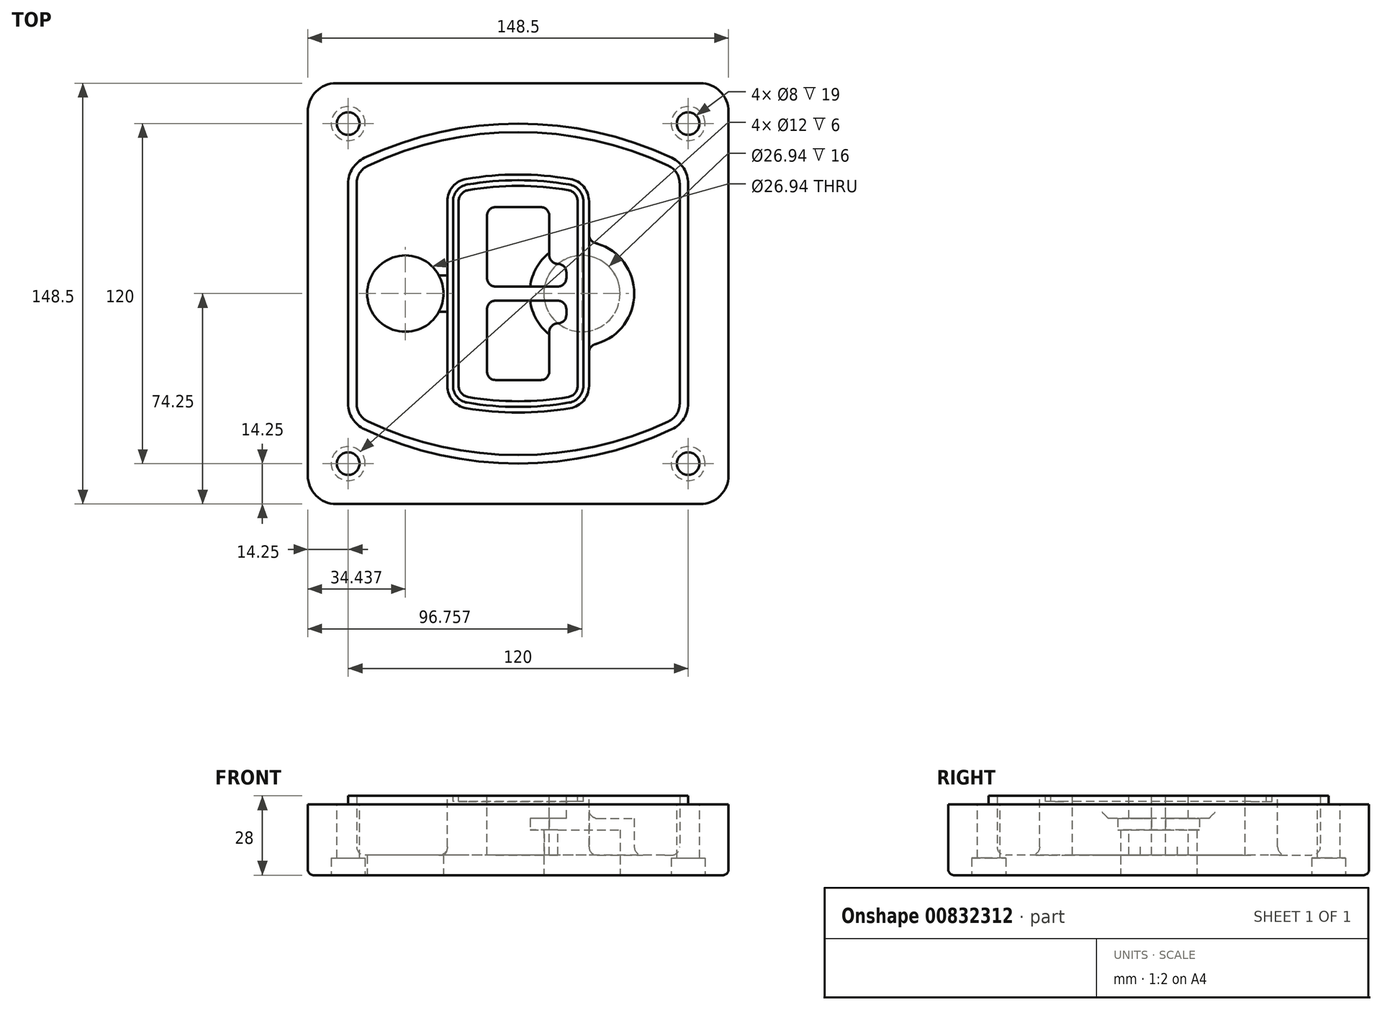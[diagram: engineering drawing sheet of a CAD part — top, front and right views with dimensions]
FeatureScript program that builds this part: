
annotation { "Feature Type Name" : "Feature", "Feature Type Description" : "" }
export const myFeature = defineFeature(function(context is Context, id is Id, definition is map)
    precondition{}
    {
        {
            var Q0;
            Q0=qCreatedBy(makeId("Top.planeOp"),FACE);
            var sketch = newSketch(context, id + "F0", { "sketchPlane" : qUnion([Q0])});
            skPoint(sketch, "E0.rect.middle", {"position": v(0, 0) * mm});
            skLineSegment(sketch, "E1.bottom", {"start": v(-64.25, -74.25) * mm, "end": v(64.25, -74.25) * mm});
            skLineSegment(sketch, "E1.top", {"start": v(-64.25, 74.25) * mm, "end": v(64.25, 74.25) * mm});
            skLineSegment(sketch, "E1.left", {"start": v(-74.25, -64.25) * mm, "end": v(-74.25, 64.25) * mm});
            skLineSegment(sketch, "E1.right", {"start": v(74.25, -64.25) * mm, "end": v(74.25, 64.25) * mm});
            skLineSegment(sketch, "E2", {"start": v(-74.25, 74.25) * mm, "end": v(74.25, -74.25) * mm, "construction": true});
            skLineSegment(sketch, "E3", {"start": v(74.25, 74.25) * mm, "end": v(-74.25, -74.25) * mm, "construction": true});
            skCircle(sketch, "E4", {"center": v(-60, 60) * mm, "radius": 4 * mm});
            skCircle(sketch, "E5", {"center": v(60, 60) * mm, "radius": 4 * mm});
            skCircle(sketch, "E6", {"center": v(60, -60) * mm, "radius": 4 * mm});
            skCircle(sketch, "E7", {"center": v(-60, -60) * mm, "radius": 4 * mm});
            skLineSegment(sketch, "E8", {"start": v(-60, 60) * mm, "end": v(60, 60) * mm, "construction": true});
            skLineSegment(sketch, "E9", {"start": v(60, 60) * mm, "end": v(60, -60) * mm, "construction": true});
            skLineSegment(sketch, "E10", {"start": v(60, -60) * mm, "end": v(-60, -60) * mm, "construction": true});
            skLineSegment(sketch, "E11", {"start": v(-60, -60) * mm, "end": v(-60, 60) * mm, "construction": true});
            skLineSegment(sketch, "E12", {"start": v(-60, 38.83) * mm, "end": v(-60, -38.83) * mm});
            skLineSegment(sketch, "E13", {"start": v(60, 38.83) * mm, "end": v(60, -38.83) * mm});
            skArc(sketch, "E14", {"start": v(54.26, 47.88) * mm, "mid": v(0, 60) * mm, "end": v(-54.26, 47.88) * mm});
            skArc(sketch, "E15", {"start": v(-54.26, -47.88) * mm, "mid": v(0, -60) * mm, "end": v(54.26, -47.88) * mm});
            skLineSegment(sketch, "E16", {"start": v(-60, 0) * mm, "end": v(60, 0) * mm, "construction": true});
            skPoint(sketch, "E17.visualSharp", {"position": v(-60, -45) * mm});
            skArc(sketch, "E17.filletArc", {"start": v(-60, -38.83) * mm, "mid": v(-58.44, -44.2) * mm, "end": v(-54.26, -47.88) * mm});
            skPoint(sketch, "E18.visualSharp", {"position": v(-60, 45) * mm});
            skArc(sketch, "E18.filletArc", {"start": v(-54.26, 47.88) * mm, "mid": v(-58.44, 44.2) * mm, "end": v(-60, 38.83) * mm});
            skPoint(sketch, "E19.visualSharp", {"position": v(60, 45) * mm});
            skArc(sketch, "E19.filletArc", {"start": v(60, 38.83) * mm, "mid": v(58.44, 44.2) * mm, "end": v(54.26, 47.88) * mm});
            skPoint(sketch, "E20.visualSharp", {"position": v(60, -45) * mm});
            skArc(sketch, "E20.filletArc", {"start": v(54.26, -47.88) * mm, "mid": v(58.44, -44.2) * mm, "end": v(60, -38.83) * mm});
            skPoint(sketch, "E21.visualSharp", {"position": v(-74.25, 74.25) * mm});
            skArc(sketch, "E21.filletArc", {"start": v(-64.25, 74.25) * mm, "mid": v(-71.32, 71.32) * mm, "end": v(-74.25, 64.25) * mm});
            skPoint(sketch, "E22.visualSharp", {"position": v(74.25, 74.25) * mm});
            skArc(sketch, "E22.filletArc", {"start": v(74.25, 64.25) * mm, "mid": v(71.32, 71.32) * mm, "end": v(64.25, 74.25) * mm});
            skPoint(sketch, "E23.visualSharp", {"position": v(74.25, -74.25) * mm});
            skArc(sketch, "E23.filletArc", {"start": v(64.25, -74.25) * mm, "mid": v(71.32, -71.32) * mm, "end": v(74.25, -64.25) * mm});
            skPoint(sketch, "E24.visualSharp", {"position": v(-74.25, -74.25) * mm});
            skArc(sketch, "E24.filletArc", {"start": v(-74.25, -64.25) * mm, "mid": v(-71.32, -71.32) * mm, "end": v(-64.25, -74.25) * mm});
            skArc(sketch, "E25.0", {"start": v(57, 38.83) * mm, "mid": v(55.9, 42.58) * mm, "end": v(52.98, 45.17) * mm});
            skLineSegment(sketch, "E25.1", {"start": v(57, 38.83) * mm, "end": v(57, -38.83) * mm});
            skArc(sketch, "E25.2", {"start": v(52.98, -45.17) * mm, "mid": v(55.9, -42.58) * mm, "end": v(57, -38.83) * mm});
            skArc(sketch, "E25.3", {"start": v(-52.98, -45.17) * mm, "mid": v(0, -57) * mm, "end": v(52.98, -45.17) * mm});
            skArc(sketch, "E25.4", {"start": v(-57, -38.83) * mm, "mid": v(-55.9, -42.58) * mm, "end": v(-52.98, -45.17) * mm});
            skArc(sketch, "E25.5", {"start": v(52.98, 45.17) * mm, "mid": v(0, 57) * mm, "end": v(-52.98, 45.17) * mm});
            skLineSegment(sketch, "E25.6", {"start": v(-57, 38.83) * mm, "end": v(-57, -38.83) * mm});
            skArc(sketch, "E25.7", {"start": v(-52.98, 45.17) * mm, "mid": v(-55.9, 42.58) * mm, "end": v(-57, 38.83) * mm});
            skArc(sketch, "E26.0", {"start": v(-55.96, 51.5) * mm, "mid": v(-61.82, 46.33) * mm, "end": v(-64, 38.83) * mm});
            skArc(sketch, "E26.1", {"start": v(55.96, 51.5) * mm, "mid": v(0, 64) * mm, "end": v(-55.96, 51.5) * mm});
            skArc(sketch, "E26.2", {"start": v(64, 38.83) * mm, "mid": v(61.82, 46.33) * mm, "end": v(55.96, 51.5) * mm});
            skLineSegment(sketch, "E26.3", {"start": v(64, 38.83) * mm, "end": v(64, -38.83) * mm});
            skArc(sketch, "E26.4", {"start": v(55.96, -51.5) * mm, "mid": v(61.82, -46.33) * mm, "end": v(64, -38.83) * mm});
            skLineSegment(sketch, "E26.5", {"start": v(-64, 38.83) * mm, "end": v(-64, -38.83) * mm});
            skArc(sketch, "E26.6", {"start": v(-55.96, -51.5) * mm, "mid": v(0, -64) * mm, "end": v(55.96, -51.5) * mm});
            skArc(sketch, "E26.7", {"start": v(-64, -38.83) * mm, "mid": v(-61.82, -46.33) * mm, "end": v(-55.96, -51.5) * mm});
            skSolve(sketch);
        }
        {
            var Q0;
            Q0=makeQuery(id+"F0.imprint","IMPRINT",FACE,{"disambiguationData":[TD([[makeQuery(id+"F0.imprint","IMPRINT",EDGE,{"derivedFrom":sQuery(id+"F0.wireOp",EDGE,"E1.bottom")}),1.0]])]});
            var Q1;
            Q1=makeQuery(id+"F0.imprint","IMPRINT",FACE,{"disambiguationData":[TD([[makeQuery(id+"F0.imprint","IMPRINT",EDGE,{"derivedFrom":sQuery(id+"F0.wireOp",EDGE,"E12")}),1.0]])]});
            var Q2;
            Q2=makeQuery(id+"F0.imprint","IMPRINT",FACE,{"disambiguationData":[TD([[makeQuery(id+"F0.imprint","IMPRINT",EDGE,{"derivedFrom":sQuery(id+"F0.wireOp",EDGE,"E25.0")}),1.0]])]});
            var Q3;
            Q3=makeQuery(id+"F0.imprint","IMPRINT",FACE,{"disambiguationData":[TD([[makeQuery(id+"F0.imprint","IMPRINT",EDGE,{"derivedFrom":sQuery(id+"F0.wireOp",EDGE,"E12")}),-1.0]])]});
            extrude(context, id + "F1", {"entities" : qUnion([Q0, Q1, Q2, Q3]), "oppositeDirection" : true, "depth" : 25 * mm});
        }
        {
            var Q0;
            Q0=makeQuery(id+"F0.imprint","IMPRINT",FACE,{"disambiguationData":[TD([[makeQuery(id+"F0.imprint","IMPRINT",EDGE,{"derivedFrom":sQuery(id+"F0.wireOp",EDGE,"E12")}),1.0]])]});
            extrude(context, id + "F2", {"entities" : qUnion([Q0]), "operationType" : NewBodyOperationType.ADD, "depth" : 3 * mm, "offsetDistance" : 25 * mm});
        }
        {
            var Q0;
            Q0=makeQuery(id+"F0.imprint","IMPRINT",FACE,{"disambiguationData":[TD([[makeQuery(id+"F0.imprint","IMPRINT",EDGE,{"derivedFrom":sQuery(id+"F0.wireOp",EDGE,"E25.0")}),1.0]])]});
            extrude(context, id + "F3", {"entities" : qUnion([Q0]), "operationType" : NewBodyOperationType.REMOVE, "oppositeDirection" : true, "depth" : 18 * mm});
        }
        {
            var Q0;
            Q0=makeQuery(id+"F2.opExtrude","CAP_FACE",FACE,{"disambiguationData":[OSD([sQuery(id+"F0.wireOp",EDGE,"E12"),sQuery(id+"F0.wireOp",EDGE,"E13"),sQuery(id+"F0.wireOp",EDGE,"E14"),sQuery(id+"F0.wireOp",EDGE,"E15"),sQuery(id+"F0.wireOp",EDGE,"E17.filletArc"),sQuery(id+"F0.wireOp",EDGE,"E18.filletArc"),sQuery(id+"F0.wireOp",EDGE,"E19.filletArc"),sQuery(id+"F0.wireOp",EDGE,"E20.filletArc"),sQuery(id+"F0.wireOp",EDGE,"E25.0"),sQuery(id+"F0.wireOp",EDGE,"E25.1"),sQuery(id+"F0.wireOp",EDGE,"E25.2"),sQuery(id+"F0.wireOp",EDGE,"E25.3"),sQuery(id+"F0.wireOp",EDGE,"E25.4"),sQuery(id+"F0.wireOp",EDGE,"E25.5"),sQuery(id+"F0.wireOp",EDGE,"E25.6"),sQuery(id+"F0.wireOp",EDGE,"E25.7")])],"isStart":false});
            var sketch = newSketch(context, id + "F4", { "sketchPlane" : qUnion([Q0])});
            skArc(sketch, "E27.0", {"start": v(-18.34, -40.45) * mm, "mid": v(0, -42) * mm, "end": v(18.34, -40.45) * mm});
            skArc(sketch, "E28.0", {"start": v(18.34, 40.45) * mm, "mid": v(0, 42) * mm, "end": v(-18.34, 40.45) * mm});
            skLineSegment(sketch, "E29", {"start": v(-25, 32.57) * mm, "end": v(-25, -32.57) * mm});
            skLineSegment(sketch, "E30", {"start": v(25, 32.57) * mm, "end": v(25, -32.57) * mm});
            skLineSegment(sketch, "E31", {"start": v(-25, 39.1) * mm, "end": v(25, 39.1) * mm, "construction": true});
            skLineSegment(sketch, "E32", {"start": v(-25, -39.1) * mm, "end": v(25, -39.1) * mm, "construction": true});
            skPoint(sketch, "E33.visualSharp", {"position": v(-25, 39.1) * mm});
            skArc(sketch, "E33.filletArc", {"start": v(-18.34, 40.45) * mm, "mid": v(-23.11, 37.73) * mm, "end": v(-25, 32.57) * mm});
            skPoint(sketch, "E34.visualSharp", {"position": v(25, 39.1) * mm});
            skArc(sketch, "E34.filletArc", {"start": v(25, 32.57) * mm, "mid": v(23.11, 37.73) * mm, "end": v(18.34, 40.45) * mm});
            skPoint(sketch, "E35.visualSharp", {"position": v(25, -39.1) * mm});
            skArc(sketch, "E35.filletArc", {"start": v(18.34, -40.45) * mm, "mid": v(23.11, -37.73) * mm, "end": v(25, -32.57) * mm});
            skPoint(sketch, "E36.visualSharp", {"position": v(-25, -39.1) * mm});
            skArc(sketch, "E36.filletArc", {"start": v(-25, -32.57) * mm, "mid": v(-23.11, -37.73) * mm, "end": v(-18.34, -40.45) * mm});
            skArc(sketch, "E37.0", {"start": v(52.98, 45.17) * mm, "mid": v(0, 57) * mm, "end": v(-52.98, 45.17) * mm});
            skArc(sketch, "E37.1", {"start": v(-52.98, 45.17) * mm, "mid": v(-55.9, 42.58) * mm, "end": v(-57, 38.83) * mm});
            skLineSegment(sketch, "E37.2", {"start": v(-57, 38.83) * mm, "end": v(-57, -38.83) * mm});
            skArc(sketch, "E37.3", {"start": v(-57, -38.83) * mm, "mid": v(-55.9, -42.58) * mm, "end": v(-52.98, -45.17) * mm});
            skArc(sketch, "E37.4", {"start": v(-52.98, -45.17) * mm, "mid": v(0, -57) * mm, "end": v(52.98, -45.17) * mm});
            skArc(sketch, "E37.5", {"start": v(52.98, -45.17) * mm, "mid": v(55.9, -42.58) * mm, "end": v(57, -38.83) * mm});
            skLineSegment(sketch, "E37.6", {"start": v(57, 38.83) * mm, "end": v(57, -38.83) * mm});
            skArc(sketch, "E37.7", {"start": v(57, 38.83) * mm, "mid": v(55.9, 42.58) * mm, "end": v(52.98, 45.17) * mm});
            skLineSegment(sketch, "E38.0", {"start": v(23, 32.57) * mm, "end": v(23, -32.57) * mm});
            skArc(sketch, "E38.1", {"start": v(18, -38.48) * mm, "mid": v(21.58, -36.44) * mm, "end": v(23, -32.57) * mm});
            skArc(sketch, "E38.2", {"start": v(-18, -38.48) * mm, "mid": v(0, -40) * mm, "end": v(18, -38.48) * mm});
            skArc(sketch, "E38.3", {"start": v(-23, -32.57) * mm, "mid": v(-21.58, -36.44) * mm, "end": v(-18, -38.48) * mm});
            skLineSegment(sketch, "E38.4", {"start": v(-23, 32.57) * mm, "end": v(-23, -32.57) * mm});
            skArc(sketch, "E38.5", {"start": v(23, 32.57) * mm, "mid": v(21.58, 36.44) * mm, "end": v(18, 38.48) * mm});
            skArc(sketch, "E38.6", {"start": v(-18, 38.48) * mm, "mid": v(-21.58, 36.44) * mm, "end": v(-23, 32.57) * mm});
            skArc(sketch, "E38.7", {"start": v(18, 38.48) * mm, "mid": v(0, 40) * mm, "end": v(-18, 38.48) * mm});
            skArc(sketch, "E39.0", {"start": v(21, 32.57) * mm, "mid": v(20.06, 35.15) * mm, "end": v(17.67, 36.5) * mm});
            skLineSegment(sketch, "E39.1", {"start": v(21, 32.57) * mm, "end": v(21, -32.57) * mm});
            skArc(sketch, "E39.2", {"start": v(17.67, -36.5) * mm, "mid": v(20.06, -35.15) * mm, "end": v(21, -32.57) * mm});
            skArc(sketch, "E39.3", {"start": v(-17.67, -36.5) * mm, "mid": v(0, -38) * mm, "end": v(17.67, -36.5) * mm});
            skArc(sketch, "E39.4", {"start": v(-21, -32.57) * mm, "mid": v(-20.06, -35.15) * mm, "end": v(-17.67, -36.5) * mm});
            skArc(sketch, "E39.5", {"start": v(17.67, 36.5) * mm, "mid": v(0, 38) * mm, "end": v(-17.67, 36.5) * mm});
            skLineSegment(sketch, "E39.6", {"start": v(-21, 32.57) * mm, "end": v(-21, -32.57) * mm});
            skArc(sketch, "E39.7", {"start": v(-17.67, 36.5) * mm, "mid": v(-20.06, 35.15) * mm, "end": v(-21, 32.57) * mm});
            skLineSegment(sketch, "E40", {"start": v(-25, 0) * mm, "end": v(25, 0) * mm, "construction": true});
            skLineSegment(sketch, "E41", {"start": v(-11, 5.5) * mm, "end": v(-11, 27.5) * mm});
            skLineSegment(sketch, "E42", {"start": v(-8, 30.5) * mm, "end": v(8, 30.5) * mm});
            skLineSegment(sketch, "E43", {"start": v(11, 27.5) * mm, "end": v(11, 13.5) * mm});
            skLineSegment(sketch, "E44", {"start": v(14, 10.5) * mm, "end": v(14, 10.5) * mm});
            skLineSegment(sketch, "E45", {"start": v(17, 7.5) * mm, "end": v(17, 5.5) * mm});
            skLineSegment(sketch, "E46", {"start": v(14, 2.5) * mm, "end": v(-8, 2.5) * mm});
            skPoint(sketch, "E47.visualSharp", {"position": v(-11, 30.5) * mm});
            skArc(sketch, "E47.filletArc", {"start": v(-8, 30.5) * mm, "mid": v(-10.12, 29.62) * mm, "end": v(-11, 27.5) * mm});
            skPoint(sketch, "E48.visualSharp", {"position": v(11, 30.5) * mm});
            skArc(sketch, "E48.filletArc", {"start": v(11, 27.5) * mm, "mid": v(10.12, 29.62) * mm, "end": v(8, 30.5) * mm});
            skPoint(sketch, "E49.visualSharp", {"position": v(11, 10.5) * mm});
            skArc(sketch, "E49.filletArc", {"start": v(11, 13.5) * mm, "mid": v(11.88, 11.38) * mm, "end": v(14, 10.5) * mm});
            skPoint(sketch, "E50.visualSharp", {"position": v(17, 10.5) * mm});
            skArc(sketch, "E50.filletArc", {"start": v(17, 7.5) * mm, "mid": v(16.12, 9.62) * mm, "end": v(14, 10.5) * mm});
            skPoint(sketch, "E51.visualSharp", {"position": v(17, 2.5) * mm});
            skArc(sketch, "E51.filletArc", {"start": v(14, 2.5) * mm, "mid": v(16.12, 3.38) * mm, "end": v(17, 5.5) * mm});
            skPoint(sketch, "E52.visualSharp", {"position": v(-11, 2.5) * mm});
            skArc(sketch, "E52.filletArc", {"start": v(-11, 5.5) * mm, "mid": v(-10.12, 3.38) * mm, "end": v(-8, 2.5) * mm});
            skLineSegment(sketch, "E53.0.MirrorCS", {"start": v(14, -2.5) * mm, "end": v(-8, -2.5) * mm});
            skArc(sketch, "E54.0.MirrorCS", {"start": v(-11, -5.5) * mm, "mid": v(-10.12, -3.38) * mm, "end": v(-8, -2.5) * mm});
            skLineSegment(sketch, "E55.0.MirrorCS", {"start": v(-11, -5.5) * mm, "end": v(-11, -27.5) * mm});
            skArc(sketch, "E56.0.MirrorCS", {"start": v(-8, -30.5) * mm, "mid": v(-10.12, -29.62) * mm, "end": v(-11, -27.5) * mm});
            skLineSegment(sketch, "E57.0.MirrorCS", {"start": v(-8, -30.5) * mm, "end": v(8, -30.5) * mm});
            skArc(sketch, "E58.0.MirrorCS", {"start": v(11, -27.5) * mm, "mid": v(10.12, -29.62) * mm, "end": v(8, -30.5) * mm});
            skLineSegment(sketch, "E59.0.MirrorCS", {"start": v(11, -27.5) * mm, "end": v(11, -13.5) * mm});
            skArc(sketch, "E60.0.MirrorCS", {"start": v(11, -13.5) * mm, "mid": v(11.88, -11.38) * mm, "end": v(14, -10.5) * mm});
            skArc(sketch, "E61.0.MirrorCS", {"start": v(17, -7.5) * mm, "mid": v(16.12, -9.62) * mm, "end": v(14, -10.5) * mm});
            skLineSegment(sketch, "E62.0.MirrorCS", {"start": v(17, -7.5) * mm, "end": v(17, -5.5) * mm});
            skArc(sketch, "E63.0.MirrorCS", {"start": v(14, -2.5) * mm, "mid": v(16.12, -3.38) * mm, "end": v(17, -5.5) * mm});
            skSolve(sketch);
        }
        {
            var Q0;
            Q0=makeQuery(id+"F4.imprint","IMPRINT",FACE,{"disambiguationData":[TD([[makeQuery(id+"F4.imprint","IMPRINT",EDGE,{"derivedFrom":sQuery(id+"F4.wireOp",EDGE,"E27.0")}),1.0]])]});
            var Q1;
            Q1=makeQuery(id+"F4.imprint","IMPRINT",FACE,{"disambiguationData":[TD([[makeQuery(id+"F4.imprint","IMPRINT",EDGE,{"derivedFrom":sQuery(id+"F4.wireOp",EDGE,"E38.0")}),-1.0]])]});
            var Q2;
            Q2=makeQuery(id+"F4.imprint","IMPRINT",FACE,{"disambiguationData":[TD([[makeQuery(id+"F4.imprint","IMPRINT",EDGE,{"derivedFrom":sQuery(id+"F4.wireOp",EDGE,"E39.0")}),1.0]])]});
            extrude(context, id + "F5", {"entities" : qUnion([Q0, Q1, Q2]), "operationType" : NewBodyOperationType.ADD, "endBound" : BoundingType.UP_TO_NEXT, "oppositeDirection" : true, "depth" : 25 * mm});
        }
        {
            var Q0;
            Q0=makeQuery(id+"F4.imprint","IMPRINT",FACE,{"disambiguationData":[TD([[makeQuery(id+"F4.imprint","IMPRINT",EDGE,{"derivedFrom":sQuery(id+"F4.wireOp",EDGE,"E38.0")}),-1.0]])]});
            extrude(context, id + "F6", {"entities" : qUnion([Q0]), "operationType" : NewBodyOperationType.REMOVE, "oppositeDirection" : true, "depth" : 2 * mm});
        }
        {
            var Q0;
            Q0=makeQuery(id+"F1.opExtrude","CAP_FACE",FACE,{"disambiguationData":[OSD([sQuery(id+"F0.wireOp",EDGE,"E1.bottom"),sQuery(id+"F0.wireOp",EDGE,"E1.top"),sQuery(id+"F0.wireOp",EDGE,"E1.left"),sQuery(id+"F0.wireOp",EDGE,"E1.right"),sQuery(id+"F0.wireOp",EDGE,"E4"),sQuery(id+"F0.wireOp",EDGE,"E5"),sQuery(id+"F0.wireOp",EDGE,"E6"),sQuery(id+"F0.wireOp",EDGE,"E7"),sQuery(id+"F0.wireOp",EDGE,"E21.filletArc"),sQuery(id+"F0.wireOp",EDGE,"E22.filletArc"),sQuery(id+"F0.wireOp",EDGE,"E23.filletArc"),sQuery(id+"F0.wireOp",EDGE,"E24.filletArc")])],"isStart":false});
            var sketch = newSketch(context, id + "F7", { "sketchPlane" : qUnion([Q0])});
            skCircle(sketch, "E64", {"center": v(22.5, 0) * mm, "radius": 13.47 * mm});
            skCircle(sketch, "E65", {"center": v(-39.81, 0) * mm, "radius": 13.47 * mm});
            skLineSegment(sketch, "E66", {"start": v(74.25, 0) * mm, "end": v(-74.25, 0) * mm});
            skCircle(sketch, "E67", {"center": v(22.5, 0) * mm, "radius": 18.47 * mm});
            skCircle(sketch, "E68", {"center": v(60, -60) * mm, "radius": 6 * mm});
            skCircle(sketch, "E69", {"center": v(-60, -60) * mm, "radius": 6 * mm});
            skCircle(sketch, "E70", {"center": v(-60, 60) * mm, "radius": 6 * mm});
            skCircle(sketch, "E71", {"center": v(60, 60) * mm, "radius": 6 * mm});
            skSolve(sketch);
        }
        {
            var Q0;
            {var subQ1=sQuery(id+"F7.wireOp",EDGE,"E66");var subQ4=sQuery(id+"F7.wireOp",EDGE,"E64");var subQ6=makeQuery(id+"F7.imprint","INTERSECT",VERTEX,{"disambiguationData":[OD(0.0)],"derivedFrom":[subQ4,subQ1]});Q0=makeQuery(id+"F7.imprint","IMPRINT",FACE,{"disambiguationData":[TD([[makeQuery(id+"F7.imprint","IMPRINT",EDGE,{"disambiguationData":[TD([[subQ6,-1.0]])],"derivedFrom":subQ4}),-1.0]])]});}
            var Q1;
            {var subQ0=sQuery(id+"F7.wireOp",EDGE,"E66");var subQ1=sQuery(id+"F7.wireOp",EDGE,"E64");var subQ3=makeQuery(id+"F7.imprint","INTERSECT",VERTEX,{"disambiguationData":[OD(0.0)],"derivedFrom":[subQ1,subQ0]});Q1=makeQuery(id+"F7.imprint","IMPRINT",FACE,{"disambiguationData":[TD([[makeQuery(id+"F7.imprint","IMPRINT",EDGE,{"disambiguationData":[TD([[subQ3,-1.0]])],"derivedFrom":subQ1}),1.0]])]});}
            var Q2;
            {var subQ0=sQuery(id+"F7.wireOp",EDGE,"E66");var subQ1=sQuery(id+"F7.wireOp",EDGE,"E64");var subQ3=makeQuery(id+"F7.imprint","INTERSECT",VERTEX,{"disambiguationData":[OD(0.0)],"derivedFrom":[subQ1,subQ0]});Q2=makeQuery(id+"F7.imprint","IMPRINT",FACE,{"disambiguationData":[TD([[makeQuery(id+"F7.imprint","IMPRINT",EDGE,{"disambiguationData":[TD([[subQ3,1.0]])],"derivedFrom":subQ1}),1.0]])]});}
            var Q3;
            {var subQ1=sQuery(id+"F7.wireOp",EDGE,"E66");var subQ4=sQuery(id+"F7.wireOp",EDGE,"E64");var subQ6=makeQuery(id+"F7.imprint","INTERSECT",VERTEX,{"disambiguationData":[OD(0.0)],"derivedFrom":[subQ4,subQ1]});Q3=makeQuery(id+"F7.imprint","IMPRINT",FACE,{"disambiguationData":[TD([[makeQuery(id+"F7.imprint","IMPRINT",EDGE,{"disambiguationData":[TD([[subQ6,1.0]])],"derivedFrom":subQ4}),-1.0]])]});}
            extrude(context, id + "F8", {"entities" : qUnion([Q0, Q1, Q2, Q3]), "operationType" : NewBodyOperationType.ADD, "oppositeDirection" : true, "depth" : 20 * mm});
        }
        {
            var Q0;
            {var subQ0=sQuery(id+"F7.wireOp",EDGE,"E66");var subQ1=sQuery(id+"F7.wireOp",EDGE,"E64");var subQ3=makeQuery(id+"F7.imprint","INTERSECT",VERTEX,{"disambiguationData":[OD(0.0)],"derivedFrom":[subQ1,subQ0]});Q0=makeQuery(id+"F7.imprint","IMPRINT",FACE,{"disambiguationData":[TD([[makeQuery(id+"F7.imprint","IMPRINT",EDGE,{"disambiguationData":[TD([[subQ3,-1.0]])],"derivedFrom":subQ1}),1.0]])]});}
            var Q1;
            {var subQ0=sQuery(id+"F7.wireOp",EDGE,"E66");var subQ1=sQuery(id+"F7.wireOp",EDGE,"E64");var subQ3=makeQuery(id+"F7.imprint","INTERSECT",VERTEX,{"disambiguationData":[OD(0.0)],"derivedFrom":[subQ1,subQ0]});Q1=makeQuery(id+"F7.imprint","IMPRINT",FACE,{"disambiguationData":[TD([[makeQuery(id+"F7.imprint","IMPRINT",EDGE,{"disambiguationData":[TD([[subQ3,1.0]])],"derivedFrom":subQ1}),1.0]])]});}
            extrude(context, id + "F9", {"entities" : qUnion([Q0, Q1]), "operationType" : NewBodyOperationType.REMOVE, "oppositeDirection" : true, "depth" : 16 * mm});
        }
        {
            var Q0;
            {var subQ0=sQuery(id+"F7.wireOp",EDGE,"E66");var subQ1=sQuery(id+"F7.wireOp",EDGE,"E65");var subQ3=makeQuery(id+"F7.imprint","INTERSECT",VERTEX,{"disambiguationData":[OD(0.0)],"derivedFrom":[subQ1,subQ0]});Q0=makeQuery(id+"F7.imprint","IMPRINT",FACE,{"disambiguationData":[TD([[makeQuery(id+"F7.imprint","IMPRINT",EDGE,{"disambiguationData":[TD([[subQ3,-1.0]])],"derivedFrom":subQ1}),1.0]])]});}
            var Q1;
            {var subQ0=sQuery(id+"F7.wireOp",EDGE,"E66");var subQ1=sQuery(id+"F7.wireOp",EDGE,"E65");var subQ3=makeQuery(id+"F7.imprint","INTERSECT",VERTEX,{"disambiguationData":[OD(0.0)],"derivedFrom":[subQ1,subQ0]});Q1=makeQuery(id+"F7.imprint","IMPRINT",FACE,{"disambiguationData":[TD([[makeQuery(id+"F7.imprint","IMPRINT",EDGE,{"disambiguationData":[TD([[subQ3,1.0]])],"derivedFrom":subQ1}),1.0]])]});}
            extrude(context, id + "F10", {"entities" : qUnion([Q0, Q1]), "operationType" : NewBodyOperationType.REMOVE, "oppositeDirection" : true, "depth" : 25 * mm});
        }
        {
            var Q0;
            Q0=makeQuery(id+"F7.imprint","IMPRINT",FACE,{"disambiguationData":[TD([[makeQuery(id+"F7.imprint","IMPRINT",EDGE,{"derivedFrom":sQuery(id+"F7.wireOp",EDGE,"E68")}),1.0]])]});
            var Q1;
            Q1=makeQuery(id+"F7.imprint","IMPRINT",FACE,{"disambiguationData":[TD([[makeQuery(id+"F7.imprint","IMPRINT",EDGE,{"derivedFrom":makeQuery(id+"F1.opExtrude","CAP_EDGE",EDGE,{"disambiguationData":[OSD([sQuery(id+"F0.wireOp",EDGE,"E5")])],"isStart":false})}),-1.0]])]});
            var Q2;
            Q2=makeQuery(id+"F7.imprint","IMPRINT",FACE,{"disambiguationData":[TD([[makeQuery(id+"F7.imprint","IMPRINT",EDGE,{"derivedFrom":sQuery(id+"F7.wireOp",EDGE,"E69")}),1.0]])]});
            var Q3;
            Q3=makeQuery(id+"F7.imprint","IMPRINT",FACE,{"disambiguationData":[TD([[makeQuery(id+"F7.imprint","IMPRINT",EDGE,{"derivedFrom":makeQuery(id+"F1.opExtrude","CAP_EDGE",EDGE,{"disambiguationData":[OSD([sQuery(id+"F0.wireOp",EDGE,"E4")])],"isStart":false})}),-1.0]])]});
            var Q4;
            Q4=makeQuery(id+"F7.imprint","IMPRINT",FACE,{"disambiguationData":[TD([[makeQuery(id+"F7.imprint","IMPRINT",EDGE,{"derivedFrom":sQuery(id+"F7.wireOp",EDGE,"E70")}),1.0]])]});
            var Q5;
            Q5=makeQuery(id+"F7.imprint","IMPRINT",FACE,{"disambiguationData":[TD([[makeQuery(id+"F7.imprint","IMPRINT",EDGE,{"derivedFrom":makeQuery(id+"F1.opExtrude","CAP_EDGE",EDGE,{"disambiguationData":[OSD([sQuery(id+"F0.wireOp",EDGE,"E7")])],"isStart":false})}),-1.0]])]});
            var Q6;
            Q6=makeQuery(id+"F7.imprint","IMPRINT",FACE,{"disambiguationData":[TD([[makeQuery(id+"F7.imprint","IMPRINT",EDGE,{"derivedFrom":sQuery(id+"F7.wireOp",EDGE,"E71")}),1.0]])]});
            var Q7;
            Q7=makeQuery(id+"F7.imprint","IMPRINT",FACE,{"disambiguationData":[TD([[makeQuery(id+"F7.imprint","IMPRINT",EDGE,{"derivedFrom":makeQuery(id+"F1.opExtrude","CAP_EDGE",EDGE,{"disambiguationData":[OSD([sQuery(id+"F0.wireOp",EDGE,"E6")])],"isStart":false})}),-1.0]])]});
            extrude(context, id + "F11", {"entities" : qUnion([Q0, Q1, Q2, Q3, Q4, Q5, Q6, Q7]), "operationType" : NewBodyOperationType.REMOVE, "oppositeDirection" : true, "depth" : 6 * mm});
        }
        {
            var Q0;
            Q0=makeQuery(id+"F9.boolean.opBoolean","COPY",FACE,{"derivedFrom":makeQuery(id+"F9.opExtrude","CAP_FACE",FACE,{"disambiguationData":[OSD([sQuery(id+"F7.wireOp",EDGE,"E64")])],"isStart":false})});
            var sketch = newSketch(context, id + "F12", { "sketchPlane" : qUnion([Q0])});
            skArc(sketch, "E72.0", {"start": v(11, 14.45) * mm, "mid": v(6.45, 9.13) * mm, "end": v(4.2, 2.5) * mm});
            skArc(sketch, "E72.1", {"start": v(4.2, -2.5) * mm, "mid": v(6.45, -9.13) * mm, "end": v(11, -14.45) * mm});
            skLineSegment(sketch, "E73", {"start": v(4.2, -2.5) * mm, "end": v(14, -2.5) * mm});
            skLineSegment(sketch, "E74.0", {"start": v(14, 2.5) * mm, "end": v(4.2, 2.5) * mm});
            skArc(sketch, "E74.1", {"start": v(14, 2.5) * mm, "mid": v(16.12, 3.38) * mm, "end": v(17, 5.5) * mm});
            skLineSegment(sketch, "E74.2", {"start": v(17, 7.5) * mm, "end": v(17, 5.5) * mm});
            skArc(sketch, "E74.3", {"start": v(17, 7.5) * mm, "mid": v(16.12, 9.62) * mm, "end": v(14, 10.5) * mm});
            skArc(sketch, "E74.4", {"start": v(11, 13.5) * mm, "mid": v(11.88, 11.38) * mm, "end": v(14, 10.5) * mm});
            skLineSegment(sketch, "E74.5", {"start": v(11, 14.45) * mm, "end": v(11, 13.5) * mm});
            skLineSegment(sketch, "E74.7", {"start": v(14, -2.5) * mm, "end": v(4.2, -2.5) * mm});
            skArc(sketch, "E74.8", {"start": v(14, -2.5) * mm, "mid": v(16.12, -3.38) * mm, "end": v(17, -5.5) * mm});
            skLineSegment(sketch, "E74.9", {"start": v(17, -7.5) * mm, "end": v(17, -5.5) * mm});
            skArc(sketch, "E74.10", {"start": v(17, -7.5) * mm, "mid": v(16.12, -9.62) * mm, "end": v(14, -10.5) * mm});
            skArc(sketch, "E74.11", {"start": v(11, -13.5) * mm, "mid": v(11.88, -11.38) * mm, "end": v(14, -10.5) * mm});
            skLineSegment(sketch, "E74.12", {"start": v(11, -14.45) * mm, "end": v(11, -13.5) * mm});
            skPoint(sketch, "E75.orphan", {"position": v(11, -27.5) * mm});
            skPoint(sketch, "E76.orphan", {"position": v(-8, -2.5) * mm});
            skPoint(sketch, "E77.orphan", {"position": v(-8, 2.5) * mm});
            skPoint(sketch, "E78.orphan", {"position": v(11, 27.5) * mm});
            skSolve(sketch);
        }
        {
            var Q0;
            {var subQ7=sQuery(id+"F12.wireOp",EDGE,"E72.0");var subQ14=sQuery(id+"F12.wireOp",EDGE,"E72.1");var subQ16=sQuery(id+"F12.wireOp",EDGE,"E74.1");var subQ18=sQuery(id+"F12.wireOp",EDGE,"E74.8");Q0=qUnion([makeQuery(id+"F12.imprint","IMPRINT",FACE,{"disambiguationData":[TD([[makeQuery(id+"F12.imprint","IMPRINT",EDGE,{"derivedFrom":subQ7}),1.0]])]}),makeQuery(id+"F12.imprint","IMPRINT",FACE,{"disambiguationData":[TD([[makeQuery(id+"F12.imprint","IMPRINT",EDGE,{"derivedFrom":subQ14}),1.0]])]}),makeQuery(id+"F12.imprint","IMPRINT",FACE,{"disambiguationData":[TD([[makeQuery(id+"F12.imprint","IMPRINT",EDGE,{"derivedFrom":subQ16}),1.0]])]}),makeQuery(id+"F12.imprint","IMPRINT",FACE,{"disambiguationData":[TD([[makeQuery(id+"F12.imprint","IMPRINT",EDGE,{"derivedFrom":subQ18}),-1.0]])]})]);}
            var Q1;
            Q1=makeQuery(id+"F5.boolean.opBoolean","SPLIT",FACE,{"disambiguationData":[TD([makeQuery(id+"F5.opExtrude","SWEPT_FACE",FACE,{"disambiguationData":[OSD([sQuery(id+"F4.wireOp",EDGE,"E41")])]})])],"derivedFrom":makeQuery(id+"F3.boolean.opBoolean","COPY",FACE,{"derivedFrom":makeQuery(id+"F3.opExtrude","CAP_FACE",FACE,{"disambiguationData":[OSD([sQuery(id+"F0.wireOp",EDGE,"E25.0"),sQuery(id+"F0.wireOp",EDGE,"E25.1"),sQuery(id+"F0.wireOp",EDGE,"E25.2"),sQuery(id+"F0.wireOp",EDGE,"E25.3"),sQuery(id+"F0.wireOp",EDGE,"E25.4"),sQuery(id+"F0.wireOp",EDGE,"E25.5"),sQuery(id+"F0.wireOp",EDGE,"E25.6"),sQuery(id+"F0.wireOp",EDGE,"E25.7")])],"isStart":false})})});
            extrude(context, id + "F13", {"entities" : qUnion([Q0]), "operationType" : NewBodyOperationType.REMOVE, "endBound" : BoundingType.UP_TO_SURFACE, "endBoundEntityFace" : qUnion([Q1]), "depth" : 25 * mm});
        }
        {
            var Q0;
            Q0=makeQuery(id+"F3.boolean.opBoolean","COPY",EDGE,{"derivedFrom":makeQuery(id+"F3.opExtrude","CAP_EDGE",EDGE,{"disambiguationData":[OSD([sQuery(id+"F0.wireOp",EDGE,"E25.6")])],"isStart":false})});
            var Q1;
            Q1=makeQuery(id+"F8.boolean.opBoolean","INTERSECT",EDGE,{"derivedFrom":[makeQuery(id+"F5.opExtrude","SWEPT_FACE",FACE,{"disambiguationData":[OSD([sQuery(id+"F4.wireOp",EDGE,"E30")])]}),makeQuery(id+"F8.opExtrude","CAP_FACE",FACE,{"disambiguationData":[OSD([sQuery(id+"F7.wireOp",EDGE,"E67")])],"isStart":false})]});
            var Q2;
            Q2=makeQuery(id+"F8.boolean.opBoolean","INTERSECT",EDGE,{"disambiguationData":[OD(1.0)],"derivedFrom":[makeQuery(id+"F5.opExtrude","SWEPT_FACE",FACE,{"disambiguationData":[OSD([sQuery(id+"F4.wireOp",EDGE,"E30")])]}),makeQuery(id+"F8.opExtrude","SWEPT_FACE",FACE,{"disambiguationData":[OSD([sQuery(id+"F7.wireOp",EDGE,"E67")])]})]});
            var Q3;
            {var subQ0=sQuery(id+"F4.wireOp",EDGE,"E30");Q3=makeQuery(id+"F8.boolean.opBoolean","SPLIT",EDGE,{"disambiguationData":[TD([makeQuery(id+"F5.opExtrude","SWEPT_FACE",FACE,{"disambiguationData":[OSD([sQuery(id+"F4.wireOp",EDGE,"E35.filletArc")])]})])],"derivedFrom":makeQuery(id+"F5.opExtrude","CAP_EDGE",EDGE,{"disambiguationData":[OSD([subQ0])],"isStart":false})});}
            var Q4;
            {var subQ0=sQuery(id+"F0.wireOp",EDGE,"E25.7");var subQ1=sQuery(id+"F0.wireOp",EDGE,"E25.1");var subQ2=sQuery(id+"F0.wireOp",EDGE,"E25.6");var subQ3=sQuery(id+"F0.wireOp",EDGE,"E25.5");var subQ4=sQuery(id+"F0.wireOp",EDGE,"E25.4");var subQ5=sQuery(id+"F0.wireOp",EDGE,"E25.0");var subQ6=sQuery(id+"F0.wireOp",EDGE,"E25.2");var subQ7=sQuery(id+"F0.wireOp",EDGE,"E25.3");Q4=makeQuery(id+"F8.boolean.opBoolean","INTERSECT",EDGE,{"derivedFrom":[makeQuery(id+"F5.boolean.opBoolean","SPLIT",FACE,{"disambiguationData":[TD([makeQuery(id+"F2.opExtrude","SWEPT_FACE",FACE,{"disambiguationData":[OSD([subQ5])]})])],"derivedFrom":makeQuery(id+"F3.boolean.opBoolean","COPY",FACE,{"derivedFrom":makeQuery(id+"F3.opExtrude","CAP_FACE",FACE,{"disambiguationData":[OSD([subQ5,subQ1,subQ6,subQ7,subQ4,subQ3,subQ2,subQ0])],"isStart":false})})}),makeQuery(id+"F8.opExtrude","SWEPT_FACE",FACE,{"disambiguationData":[OSD([sQuery(id+"F7.wireOp",EDGE,"E67")])]})]});}
            var Q5;
            Q5=makeQuery(id+"F8.boolean.opBoolean","INTERSECT",EDGE,{"disambiguationData":[OD(0.0)],"derivedFrom":[makeQuery(id+"F5.opExtrude","SWEPT_FACE",FACE,{"disambiguationData":[OSD([sQuery(id+"F4.wireOp",EDGE,"E30")])]}),makeQuery(id+"F8.opExtrude","SWEPT_FACE",FACE,{"disambiguationData":[OSD([sQuery(id+"F7.wireOp",EDGE,"E67")])]})]});
            fillet(context, id + "F14", {"entities" : qUnion([Q0, Q1, Q2, Q3, Q4, Q5]), "radius" : 3 * mm, "tangentPropagation" : true, "allowEdgeOverflow" : false});
        }
        {
            var Q0;
            Q0=makeQuery(id+"F1.opExtrude","CAP_EDGE",EDGE,{"disambiguationData":[OSD([sQuery(id+"F0.wireOp",EDGE,"E1.bottom")])],"isStart":false});
            fillet(context, id + "F15", {"entities" : qUnion([Q0]), "radius" : 2 * mm, "tangentPropagation" : true, "allowEdgeOverflow" : false});
        }
    });
